# Revit family: Pump_Dewatering-Effluent-Zoeller-98_Automatic_Series
name_source: partatom
category: Mechanical Equipment
revit_build: Autodesk Revit 2014 (Build: 20130308_1515(x64)
units: mm (PartAtom-declared; Revit-internal decimal feet)

## types (2) — shared parameters
Assembly Code = D2010900
Cooling = Oil Filled
Cord Length = 180"
Cord Type = UL Listed
Default Elevation = 0"
Description = Automatic Effluent or dewatering submersible pumps for septic tanks, low pressure pipe (LPP) and enhanced flow STEP systems.
Discharge Diameter = 1 1/2" NPT
Discharge Height = 3 15/16"
Discharge Radius = 3/4"
Height = 12 1/16"
Hertz = 60
Impeller Type = Non-clogging vortex
Installation Type = Floor Mounted
Length = 7 7/8"
Manufacturer = Zoeller
Material = Cast Iron-Zoeller-Powder Coated Epoxy
Max Flow @ 5' = 72 GPM
Max. Water Temp. = 130 °F
Maximum Head = 276"
Model = 98
Motor = 1/2 HP
Motor Thermal Shutoff = Auto Reset Thermal Overload.
Motor Type = Submersible
O-Rings and Cover Gasket = Neoprene
Off Point = 3"
On Point = 9 1/2"
Operation = Automatic
Phase = 1
Price = Prices may vary. Please consult Manufacturer Representative for most up-to-date price list.
Product Page URL = http://www.zoellerpumps.com
RPM = 1725
Shaft Seal = Carbon and Ceramic
Solid Handling = 1/2" Spherical Solids
Type = Permanent Split Capacitor
URL = http://www.zoellerpumps.com
Warranty Information = 36 Months (Limited)
Waste Connection = Yes
Width = 10 1/8"

## per-type parameters (varying)
| type | Amps | Voltage |
| M98 - 115V 1PH | 9.4 | 115 V |
| D98 - 230V 1PH | 4.7 | 230 V |

## geometry (parser evidence)
native form markers: Sweep x3
no freeform markers — native parametric forms only
